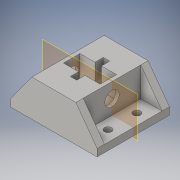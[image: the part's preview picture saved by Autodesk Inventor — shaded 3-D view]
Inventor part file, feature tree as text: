
AUTODESK INVENTOR PART (.ipt)
format: ipt  version: 2016 (Build 200138000, 138)  size: 221,696 bytes
history: native  units: in
note: dims shown in document units (in); Inventor stores cm internally (conversion verified against a paired STEP export)
features: extrude x6, sketch x6, projected_geometry x6, plane x2, fillet x2, mirror x1
ambient origin geometry x8: Origin, YZ Plane, XZ Plane, XY Plane, X Axis, Y Axis, Z Axis, Center Point
bodies: Solid1 (feature_tree)
feature tree (23):
  extrude  "Extrusion1"  Depth=1.5748in
  plane  "Work Plane1"
  extrude  "Extrusion2"  TaperAngle=0.0deg  [1 undecoded]
  extrude  "Extrusion3"  Depth=0.2in
  fillet  "Fillet1"  Radius=0.1969in
  fillet  "Fillet2"  Radius=0.2in
  extrude  "Extrusion4"  Depth=0.4in
  extrude  "Extrusion5"  Depth=1.2in TaperAngle=0.0deg
  extrude  "Extrusion6"  Depth=0.9in
  plane  "Work Plane2"
  mirror  "Mirror1"
  sketch  "Sketch1"  dims[d0=2.3622in d1=1.5748in]
  sketch  "Sketch2"  dims[d2=0.2953in d3=0.0in]
  projected_geometry  "Projected Loop1"
  sketch  "Sketch3"  dims[d4=0.1969in d5=0.2953in d6=0.1969in d7=0.2in d8=0.0in]
  projected_geometry  "Projected Loop2"
  sketch  "Sketch4"  dims[d9=1.0in d10=0.4in]
  projected_geometry  "Projected Loop3"
  sketch  "Sketch5"  dims[d11=1.0in d12=1.2in d13=0.0in]
  projected_geometry  "Projected Loop4"
  projected_geometry  "Projected Loop5"
  sketch  "Sketch6"  dims[d14=0.175in d15=0.9in d16=1.0in d17=0.45in d18=0.8in d19=0.0in d20=0.2in d21=0.4in d22=0.4in d23=90.0deg d24=0.3937in d25=4.6125in d26=0.0in d27=0.2in d28=0.0in d29=0.2in d30=0.0in]
  projected_geometry  "Projected Loop6"
note: 1 required parameter value undecoded (feature->parameter linkage not recoverable at this tier; creation-order binding heuristic only, values carry confidence <= 0.55)
